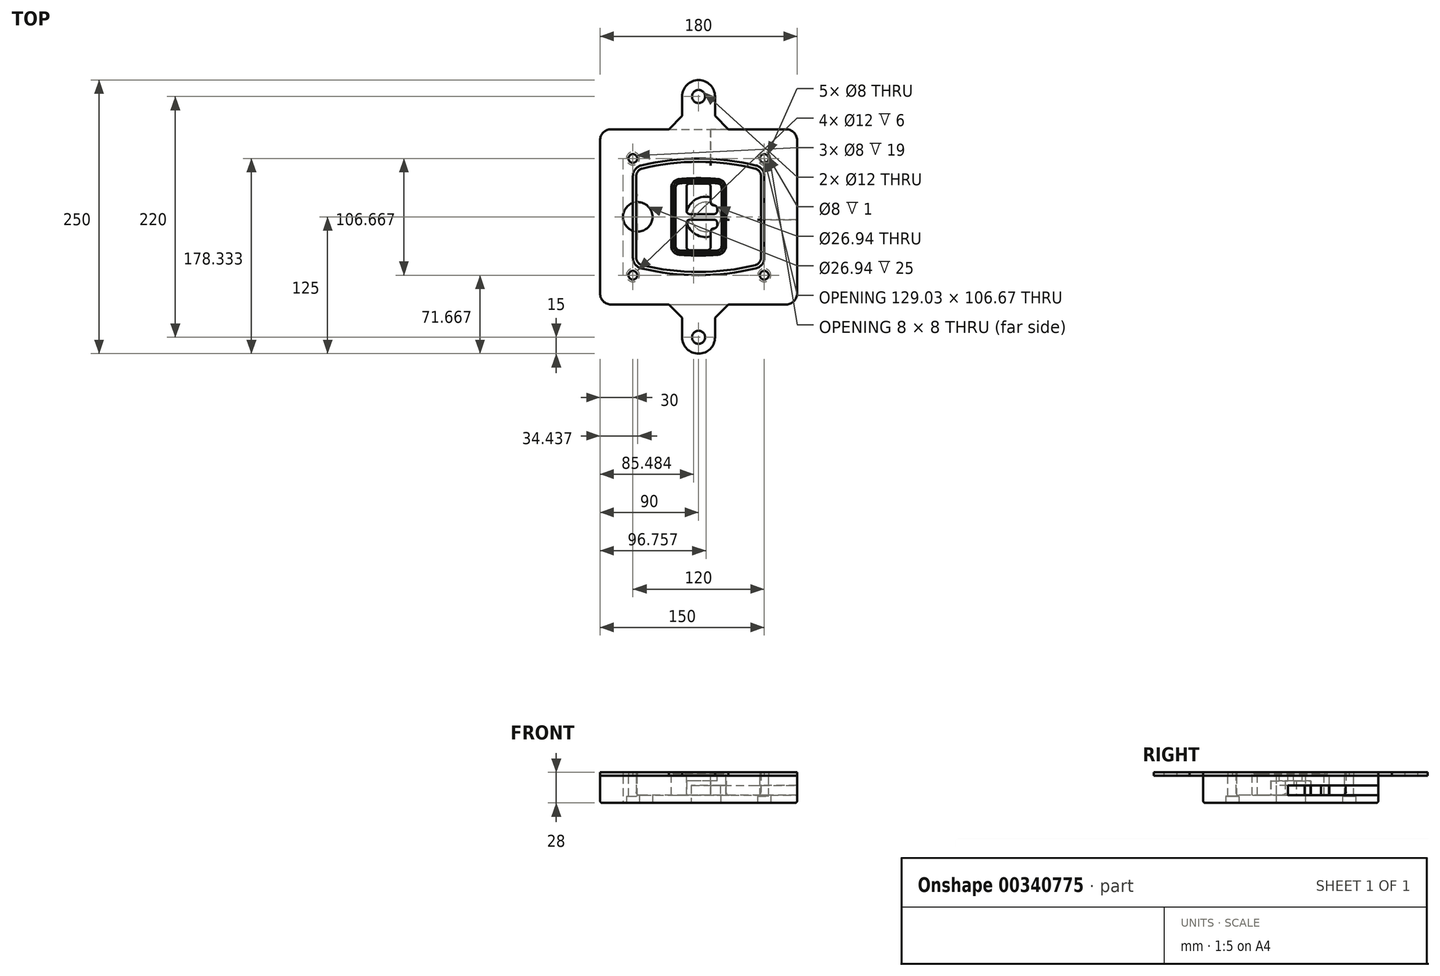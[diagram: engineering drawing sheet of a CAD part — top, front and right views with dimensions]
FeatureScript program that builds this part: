
annotation { "Feature Type Name" : "Feature", "Feature Type Description" : "" }
export const myFeature = defineFeature(function(context is Context, id is Id, definition is map)
    precondition{}
    {
        {
            var Q0;
            Q0=qCreatedBy(makeId("Top.planeOp"),FACE);
            var sketch = newSketch(context, id + "F0", { "sketchPlane" : qUnion([Q0])});
            skPoint(sketch, "E0.rect.middle", {"position": v(0, 0) * mm});
            skLineSegment(sketch, "E1.bottom", {"start": v(-80, -80) * mm, "end": v(80, -80) * mm});
            skLineSegment(sketch, "E1.top", {"start": v(-80, 80) * mm, "end": v(80, 80) * mm});
            skLineSegment(sketch, "E1.left", {"start": v(-90, -70) * mm, "end": v(-90, 70) * mm});
            skLineSegment(sketch, "E1.right", {"start": v(90, -70) * mm, "end": v(90, 70) * mm});
            skLineSegment(sketch, "E2", {"start": v(-90, 80) * mm, "end": v(90, -80) * mm, "construction": true});
            skLineSegment(sketch, "E3", {"start": v(90, 80) * mm, "end": v(-90, -80) * mm, "construction": true});
            skCircle(sketch, "E4", {"center": v(-60, 53.33) * mm, "radius": 4 * mm});
            skCircle(sketch, "E5", {"center": v(60, 53.33) * mm, "radius": 4 * mm});
            skCircle(sketch, "E6", {"center": v(60, -53.33) * mm, "radius": 4 * mm});
            skCircle(sketch, "E7", {"center": v(-60, -53.33) * mm, "radius": 4 * mm});
            skLineSegment(sketch, "E8", {"start": v(-60, 53.33) * mm, "end": v(60, 53.33) * mm, "construction": true});
            skLineSegment(sketch, "E9", {"start": v(60, 53.33) * mm, "end": v(60, -53.33) * mm, "construction": true});
            skLineSegment(sketch, "E10", {"start": v(60, -53.33) * mm, "end": v(-60, -53.33) * mm, "construction": true});
            skLineSegment(sketch, "E11", {"start": v(-60, -53.33) * mm, "end": v(-60, 53.33) * mm, "construction": true});
            skLineSegment(sketch, "E12", {"start": v(-60, 37.3) * mm, "end": v(-60, -37.3) * mm});
            skLineSegment(sketch, "E13", {"start": v(60, 37.3) * mm, "end": v(60, -37.3) * mm});
            skArc(sketch, "E14", {"start": v(52.38, 47.01) * mm, "mid": v(0, 53.33) * mm, "end": v(-52.38, 47.01) * mm});
            skArc(sketch, "E15", {"start": v(-52.38, -47.01) * mm, "mid": v(0, -53.33) * mm, "end": v(52.38, -47.01) * mm});
            skLineSegment(sketch, "E16", {"start": v(-60, 0) * mm, "end": v(60, 0) * mm, "construction": true});
            skPoint(sketch, "E17.visualSharp", {"position": v(-60, -45) * mm});
            skArc(sketch, "E17.filletArc", {"start": v(-60, -37.3) * mm, "mid": v(-57.87, -43.47) * mm, "end": v(-52.38, -47.01) * mm});
            skPoint(sketch, "E18.visualSharp", {"position": v(-60, 45) * mm});
            skArc(sketch, "E18.filletArc", {"start": v(-52.38, 47.01) * mm, "mid": v(-57.87, 43.47) * mm, "end": v(-60, 37.3) * mm});
            skPoint(sketch, "E19.visualSharp", {"position": v(60, 45) * mm});
            skArc(sketch, "E19.filletArc", {"start": v(60, 37.3) * mm, "mid": v(57.87, 43.47) * mm, "end": v(52.38, 47.01) * mm});
            skPoint(sketch, "E20.visualSharp", {"position": v(60, -45) * mm});
            skArc(sketch, "E20.filletArc", {"start": v(52.38, -47.01) * mm, "mid": v(57.87, -43.47) * mm, "end": v(60, -37.3) * mm});
            skPoint(sketch, "E21.visualSharp", {"position": v(-90, 80) * mm});
            skArc(sketch, "E21.filletArc", {"start": v(-80, 80) * mm, "mid": v(-87.07, 77.07) * mm, "end": v(-90, 70) * mm});
            skPoint(sketch, "E22.visualSharp", {"position": v(90, 80) * mm});
            skArc(sketch, "E22.filletArc", {"start": v(90, 70) * mm, "mid": v(87.07, 77.07) * mm, "end": v(80, 80) * mm});
            skPoint(sketch, "E23.visualSharp", {"position": v(90, -80) * mm});
            skArc(sketch, "E23.filletArc", {"start": v(80, -80) * mm, "mid": v(87.07, -77.07) * mm, "end": v(90, -70) * mm});
            skPoint(sketch, "E24.visualSharp", {"position": v(-90, -80) * mm});
            skArc(sketch, "E24.filletArc", {"start": v(-90, -70) * mm, "mid": v(-87.07, -77.07) * mm, "end": v(-80, -80) * mm});
            skArc(sketch, "E25.0", {"start": v(57, 37.3) * mm, "mid": v(55.5, 41.62) * mm, "end": v(51.67, 44.1) * mm});
            skLineSegment(sketch, "E25.1", {"start": v(57, 37.3) * mm, "end": v(57, -37.3) * mm});
            skArc(sketch, "E25.2", {"start": v(51.67, -44.1) * mm, "mid": v(55.5, -41.62) * mm, "end": v(57, -37.3) * mm});
            skArc(sketch, "E25.3", {"start": v(-51.67, -44.1) * mm, "mid": v(0, -50.33) * mm, "end": v(51.67, -44.1) * mm});
            skArc(sketch, "E25.4", {"start": v(-57, -37.3) * mm, "mid": v(-55.5, -41.62) * mm, "end": v(-51.67, -44.1) * mm});
            skArc(sketch, "E25.5", {"start": v(51.67, 44.1) * mm, "mid": v(0, 50.33) * mm, "end": v(-51.67, 44.1) * mm});
            skLineSegment(sketch, "E25.6", {"start": v(-57, 37.3) * mm, "end": v(-57, -37.3) * mm});
            skArc(sketch, "E25.7", {"start": v(-51.67, 44.1) * mm, "mid": v(-55.5, 41.62) * mm, "end": v(-57, 37.3) * mm});
            skArc(sketch, "E26.0", {"start": v(-53.33, 50.9) * mm, "mid": v(-61.01, 45.94) * mm, "end": v(-64, 37.3) * mm});
            skArc(sketch, "E26.1", {"start": v(53.33, 50.9) * mm, "mid": v(0, 57.33) * mm, "end": v(-53.33, 50.9) * mm});
            skArc(sketch, "E26.2", {"start": v(64, 37.3) * mm, "mid": v(61.01, 45.94) * mm, "end": v(53.33, 50.9) * mm});
            skLineSegment(sketch, "E26.3", {"start": v(64, 37.3) * mm, "end": v(64, -37.3) * mm});
            skArc(sketch, "E26.4", {"start": v(53.33, -50.9) * mm, "mid": v(61.01, -45.94) * mm, "end": v(64, -37.3) * mm});
            skLineSegment(sketch, "E26.5", {"start": v(-64, 37.3) * mm, "end": v(-64, -37.3) * mm});
            skArc(sketch, "E26.6", {"start": v(-53.33, -50.9) * mm, "mid": v(0, -57.33) * mm, "end": v(53.33, -50.9) * mm});
            skArc(sketch, "E26.7", {"start": v(-64, -37.3) * mm, "mid": v(-61.01, -45.94) * mm, "end": v(-53.33, -50.9) * mm});
            skSolve(sketch);
        }
        {
            var Q0;
            Q0=makeQuery(id+"F0.imprint","IMPRINT",FACE,{"disambiguationData":[TD([[makeQuery(id+"F0.imprint","IMPRINT",EDGE,{"derivedFrom":sQuery(id+"F0.wireOp",EDGE,"E1.bottom")}),1.0]])]});
            var Q1;
            Q1=makeQuery(id+"F0.imprint","IMPRINT",FACE,{"disambiguationData":[TD([[makeQuery(id+"F0.imprint","IMPRINT",EDGE,{"derivedFrom":sQuery(id+"F0.wireOp",EDGE,"E12")}),1.0]])]});
            var Q2;
            Q2=makeQuery(id+"F0.imprint","IMPRINT",FACE,{"disambiguationData":[TD([[makeQuery(id+"F0.imprint","IMPRINT",EDGE,{"derivedFrom":sQuery(id+"F0.wireOp",EDGE,"E25.0")}),1.0]])]});
            var Q3;
            Q3=makeQuery(id+"F0.imprint","IMPRINT",FACE,{"disambiguationData":[TD([[makeQuery(id+"F0.imprint","IMPRINT",EDGE,{"derivedFrom":sQuery(id+"F0.wireOp",EDGE,"E12")}),-1.0]])]});
            extrude(context, id + "F1", {"entities" : qUnion([Q0, Q1, Q2, Q3]), "oppositeDirection" : true, "depth" : 25 * mm});
        }
        {
            var Q0;
            Q0=makeQuery(id+"F0.imprint","IMPRINT",FACE,{"disambiguationData":[TD([[makeQuery(id+"F0.imprint","IMPRINT",EDGE,{"derivedFrom":sQuery(id+"F0.wireOp",EDGE,"E12")}),1.0]])]});
            extrude(context, id + "F2", {"entities" : qUnion([Q0]), "operationType" : NewBodyOperationType.ADD, "depth" : 3 * mm});
        }
        {
            var Q0;
            Q0=makeQuery(id+"F0.imprint","IMPRINT",FACE,{"disambiguationData":[TD([[makeQuery(id+"F0.imprint","IMPRINT",EDGE,{"derivedFrom":sQuery(id+"F0.wireOp",EDGE,"E25.0")}),1.0]])]});
            extrude(context, id + "F3", {"entities" : qUnion([Q0]), "operationType" : NewBodyOperationType.REMOVE, "oppositeDirection" : true, "depth" : 18 * mm});
        }
        {
            var Q0;
            Q0=makeQuery(id+"F2.opExtrude","CAP_FACE",FACE,{"disambiguationData":[OSD([sQuery(id+"F0.wireOp",EDGE,"E12"),sQuery(id+"F0.wireOp",EDGE,"E13"),sQuery(id+"F0.wireOp",EDGE,"E14"),sQuery(id+"F0.wireOp",EDGE,"E15"),sQuery(id+"F0.wireOp",EDGE,"E17.filletArc"),sQuery(id+"F0.wireOp",EDGE,"E18.filletArc"),sQuery(id+"F0.wireOp",EDGE,"E19.filletArc"),sQuery(id+"F0.wireOp",EDGE,"E20.filletArc"),sQuery(id+"F0.wireOp",EDGE,"E25.0"),sQuery(id+"F0.wireOp",EDGE,"E25.1"),sQuery(id+"F0.wireOp",EDGE,"E25.2"),sQuery(id+"F0.wireOp",EDGE,"E25.3"),sQuery(id+"F0.wireOp",EDGE,"E25.4"),sQuery(id+"F0.wireOp",EDGE,"E25.5"),sQuery(id+"F0.wireOp",EDGE,"E25.6"),sQuery(id+"F0.wireOp",EDGE,"E25.7")])],"isStart":false});
            var sketch = newSketch(context, id + "F4", { "sketchPlane" : qUnion([Q0])});
            skArc(sketch, "E27.0", {"start": v(-17.7, -34.56) * mm, "mid": v(0, -35.33) * mm, "end": v(17.7, -34.56) * mm});
            skArc(sketch, "E28.0", {"start": v(17.7, 34.56) * mm, "mid": v(0, 35.33) * mm, "end": v(-17.7, 34.56) * mm});
            skLineSegment(sketch, "E29", {"start": v(-25, 26.59) * mm, "end": v(-25, -26.59) * mm});
            skLineSegment(sketch, "E30", {"start": v(25, 26.59) * mm, "end": v(25, -26.59) * mm});
            skLineSegment(sketch, "E31", {"start": v(-25, 33.78) * mm, "end": v(25, 33.78) * mm, "construction": true});
            skLineSegment(sketch, "E32", {"start": v(-25, -33.78) * mm, "end": v(25, -33.78) * mm, "construction": true});
            skPoint(sketch, "E33.visualSharp", {"position": v(-25, 33.78) * mm});
            skArc(sketch, "E33.filletArc", {"start": v(-17.7, 34.56) * mm, "mid": v(-22.9, 32) * mm, "end": v(-25, 26.59) * mm});
            skPoint(sketch, "E34.visualSharp", {"position": v(25, 33.78) * mm});
            skArc(sketch, "E34.filletArc", {"start": v(25, 26.59) * mm, "mid": v(22.9, 32) * mm, "end": v(17.7, 34.56) * mm});
            skPoint(sketch, "E35.visualSharp", {"position": v(25, -33.78) * mm});
            skArc(sketch, "E35.filletArc", {"start": v(17.7, -34.56) * mm, "mid": v(22.9, -32) * mm, "end": v(25, -26.59) * mm});
            skPoint(sketch, "E36.visualSharp", {"position": v(-25, -33.78) * mm});
            skArc(sketch, "E36.filletArc", {"start": v(-25, -26.59) * mm, "mid": v(-22.9, -32) * mm, "end": v(-17.7, -34.56) * mm});
            skArc(sketch, "E37.0", {"start": v(51.67, 44.1) * mm, "mid": v(0, 50.33) * mm, "end": v(-51.67, 44.1) * mm});
            skArc(sketch, "E37.1", {"start": v(-51.67, 44.1) * mm, "mid": v(-55.5, 41.62) * mm, "end": v(-57, 37.3) * mm});
            skLineSegment(sketch, "E37.2", {"start": v(-57, 37.3) * mm, "end": v(-57, -37.3) * mm});
            skArc(sketch, "E37.3", {"start": v(-57, -37.3) * mm, "mid": v(-55.5, -41.62) * mm, "end": v(-51.67, -44.1) * mm});
            skArc(sketch, "E37.4", {"start": v(-51.67, -44.1) * mm, "mid": v(0, -50.33) * mm, "end": v(51.67, -44.1) * mm});
            skArc(sketch, "E37.5", {"start": v(51.67, -44.1) * mm, "mid": v(55.5, -41.62) * mm, "end": v(57, -37.3) * mm});
            skLineSegment(sketch, "E37.6", {"start": v(57, 37.3) * mm, "end": v(57, -37.3) * mm});
            skArc(sketch, "E37.7", {"start": v(57, 37.3) * mm, "mid": v(55.5, 41.62) * mm, "end": v(51.67, 44.1) * mm});
            skLineSegment(sketch, "E38.0", {"start": v(23, 26.59) * mm, "end": v(23, -26.59) * mm});
            skArc(sketch, "E38.1", {"start": v(17.53, -32.56) * mm, "mid": v(21.42, -30.64) * mm, "end": v(23, -26.59) * mm});
            skArc(sketch, "E38.2", {"start": v(-17.53, -32.56) * mm, "mid": v(0, -33.33) * mm, "end": v(17.53, -32.56) * mm});
            skArc(sketch, "E38.3", {"start": v(-23, -26.59) * mm, "mid": v(-21.42, -30.64) * mm, "end": v(-17.53, -32.56) * mm});
            skLineSegment(sketch, "E38.4", {"start": v(-23, 26.59) * mm, "end": v(-23, -26.59) * mm});
            skArc(sketch, "E38.5", {"start": v(23, 26.59) * mm, "mid": v(21.42, 30.64) * mm, "end": v(17.53, 32.56) * mm});
            skArc(sketch, "E38.6", {"start": v(-17.53, 32.56) * mm, "mid": v(-21.42, 30.64) * mm, "end": v(-23, 26.59) * mm});
            skArc(sketch, "E38.7", {"start": v(17.53, 32.56) * mm, "mid": v(0, 33.33) * mm, "end": v(-17.53, 32.56) * mm});
            skArc(sketch, "E39.0", {"start": v(21, 26.59) * mm, "mid": v(19.95, 29.29) * mm, "end": v(17.35, 30.57) * mm});
            skLineSegment(sketch, "E39.1", {"start": v(21, 26.59) * mm, "end": v(21, -26.59) * mm});
            skArc(sketch, "E39.2", {"start": v(17.35, -30.57) * mm, "mid": v(19.95, -29.29) * mm, "end": v(21, -26.59) * mm});
            skArc(sketch, "E39.3", {"start": v(-17.35, -30.57) * mm, "mid": v(0, -31.33) * mm, "end": v(17.35, -30.57) * mm});
            skArc(sketch, "E39.4", {"start": v(-21, -26.59) * mm, "mid": v(-19.95, -29.29) * mm, "end": v(-17.35, -30.57) * mm});
            skArc(sketch, "E39.5", {"start": v(17.35, 30.57) * mm, "mid": v(0, 31.33) * mm, "end": v(-17.35, 30.57) * mm});
            skLineSegment(sketch, "E39.6", {"start": v(-21, 26.59) * mm, "end": v(-21, -26.59) * mm});
            skArc(sketch, "E39.7", {"start": v(-17.35, 30.57) * mm, "mid": v(-19.95, 29.29) * mm, "end": v(-21, 26.59) * mm});
            skLineSegment(sketch, "E40", {"start": v(-25, 0) * mm, "end": v(25, 0) * mm, "construction": true});
            skLineSegment(sketch, "E41", {"start": v(-11, 5.5) * mm, "end": v(-11, 27.5) * mm});
            skLineSegment(sketch, "E42", {"start": v(-8, 30.5) * mm, "end": v(8, 30.5) * mm});
            skLineSegment(sketch, "E43", {"start": v(11, 27.5) * mm, "end": v(11, 13.5) * mm});
            skLineSegment(sketch, "E44", {"start": v(14, 10.5) * mm, "end": v(14, 10.5) * mm});
            skLineSegment(sketch, "E45", {"start": v(17, 7.5) * mm, "end": v(17, 5.5) * mm});
            skLineSegment(sketch, "E46", {"start": v(14, 2.5) * mm, "end": v(-8, 2.5) * mm});
            skPoint(sketch, "E47.visualSharp", {"position": v(-11, 30.5) * mm});
            skArc(sketch, "E47.filletArc", {"start": v(-8, 30.5) * mm, "mid": v(-10.12, 29.62) * mm, "end": v(-11, 27.5) * mm});
            skPoint(sketch, "E48.visualSharp", {"position": v(11, 30.5) * mm});
            skArc(sketch, "E48.filletArc", {"start": v(11, 27.5) * mm, "mid": v(10.12, 29.62) * mm, "end": v(8, 30.5) * mm});
            skPoint(sketch, "E49.visualSharp", {"position": v(11, 10.5) * mm});
            skArc(sketch, "E49.filletArc", {"start": v(11, 13.5) * mm, "mid": v(11.88, 11.38) * mm, "end": v(14, 10.5) * mm});
            skPoint(sketch, "E50.visualSharp", {"position": v(17, 10.5) * mm});
            skArc(sketch, "E50.filletArc", {"start": v(17, 7.5) * mm, "mid": v(16.12, 9.62) * mm, "end": v(14, 10.5) * mm});
            skPoint(sketch, "E51.visualSharp", {"position": v(17, 2.5) * mm});
            skArc(sketch, "E51.filletArc", {"start": v(14, 2.5) * mm, "mid": v(16.12, 3.38) * mm, "end": v(17, 5.5) * mm});
            skPoint(sketch, "E52.visualSharp", {"position": v(-11, 2.5) * mm});
            skArc(sketch, "E52.filletArc", {"start": v(-11, 5.5) * mm, "mid": v(-10.12, 3.38) * mm, "end": v(-8, 2.5) * mm});
            skLineSegment(sketch, "E53.0.MirrorCS", {"start": v(14, -2.5) * mm, "end": v(-8, -2.5) * mm});
            skArc(sketch, "E54.0.MirrorCS", {"start": v(-11, -5.5) * mm, "mid": v(-10.12, -3.38) * mm, "end": v(-8, -2.5) * mm});
            skLineSegment(sketch, "E55.0.MirrorCS", {"start": v(-11, -5.5) * mm, "end": v(-11, -27.5) * mm});
            skArc(sketch, "E56.0.MirrorCS", {"start": v(-8, -30.5) * mm, "mid": v(-10.12, -29.62) * mm, "end": v(-11, -27.5) * mm});
            skLineSegment(sketch, "E57.0.MirrorCS", {"start": v(-8, -30.5) * mm, "end": v(8, -30.5) * mm});
            skArc(sketch, "E58.0.MirrorCS", {"start": v(11, -27.5) * mm, "mid": v(10.12, -29.62) * mm, "end": v(8, -30.5) * mm});
            skLineSegment(sketch, "E59.0.MirrorCS", {"start": v(11, -27.5) * mm, "end": v(11, -13.5) * mm});
            skArc(sketch, "E60.0.MirrorCS", {"start": v(11, -13.5) * mm, "mid": v(11.88, -11.38) * mm, "end": v(14, -10.5) * mm});
            skArc(sketch, "E61.0.MirrorCS", {"start": v(17, -7.5) * mm, "mid": v(16.12, -9.62) * mm, "end": v(14, -10.5) * mm});
            skLineSegment(sketch, "E62.0.MirrorCS", {"start": v(17, -7.5) * mm, "end": v(17, -5.5) * mm});
            skArc(sketch, "E63.0.MirrorCS", {"start": v(14, -2.5) * mm, "mid": v(16.12, -3.38) * mm, "end": v(17, -5.5) * mm});
            skSolve(sketch);
        }
        {
            var Q0;
            Q0=makeQuery(id+"F4.imprint","IMPRINT",FACE,{"disambiguationData":[TD([[makeQuery(id+"F4.imprint","IMPRINT",EDGE,{"derivedFrom":sQuery(id+"F4.wireOp",EDGE,"E27.0")}),1.0]])]});
            var Q1;
            Q1=makeQuery(id+"F4.imprint","IMPRINT",FACE,{"disambiguationData":[TD([[makeQuery(id+"F4.imprint","IMPRINT",EDGE,{"derivedFrom":sQuery(id+"F4.wireOp",EDGE,"E38.0")}),-1.0]])]});
            var Q2;
            Q2=makeQuery(id+"F4.imprint","IMPRINT",FACE,{"disambiguationData":[TD([[makeQuery(id+"F4.imprint","IMPRINT",EDGE,{"derivedFrom":sQuery(id+"F4.wireOp",EDGE,"E39.0")}),1.0]])]});
            extrude(context, id + "F5", {"entities" : qUnion([Q0, Q1, Q2]), "operationType" : NewBodyOperationType.ADD, "endBound" : BoundingType.UP_TO_NEXT, "oppositeDirection" : true, "depth" : 25 * mm});
        }
        {
            var Q0;
            Q0=makeQuery(id+"F4.imprint","IMPRINT",FACE,{"disambiguationData":[TD([[makeQuery(id+"F4.imprint","IMPRINT",EDGE,{"derivedFrom":sQuery(id+"F4.wireOp",EDGE,"E38.0")}),-1.0]])]});
            extrude(context, id + "F6", {"entities" : qUnion([Q0]), "operationType" : NewBodyOperationType.REMOVE, "oppositeDirection" : true, "depth" : 2 * mm});
        }
        {
            var Q0;
            Q0=makeQuery(id+"F1.opExtrude","CAP_FACE",FACE,{"disambiguationData":[OSD([sQuery(id+"F0.wireOp",EDGE,"E1.bottom"),sQuery(id+"F0.wireOp",EDGE,"E1.top"),sQuery(id+"F0.wireOp",EDGE,"E1.left"),sQuery(id+"F0.wireOp",EDGE,"E1.right"),sQuery(id+"F0.wireOp",EDGE,"E4"),sQuery(id+"F0.wireOp",EDGE,"E5"),sQuery(id+"F0.wireOp",EDGE,"E6"),sQuery(id+"F0.wireOp",EDGE,"E7"),sQuery(id+"F0.wireOp",EDGE,"E21.filletArc"),sQuery(id+"F0.wireOp",EDGE,"E22.filletArc"),sQuery(id+"F0.wireOp",EDGE,"E23.filletArc"),sQuery(id+"F0.wireOp",EDGE,"E24.filletArc")])],"isStart":false});
            var sketch = newSketch(context, id + "F7", { "sketchPlane" : qUnion([Q0])});
            skCircle(sketch, "E64", {"center": v(6.76, 0) * mm, "radius": 13.47 * mm});
            skCircle(sketch, "E65", {"center": v(-55.56, 0) * mm, "radius": 13.47 * mm});
            skLineSegment(sketch, "E66", {"start": v(90, 0) * mm, "end": v(-90, 0) * mm});
            skCircle(sketch, "E67", {"center": v(6.76, 0) * mm, "radius": 18.47 * mm});
            skCircle(sketch, "E68", {"center": v(60, -53.33) * mm, "radius": 6 * mm});
            skCircle(sketch, "E69", {"center": v(-60, -53.33) * mm, "radius": 6 * mm});
            skCircle(sketch, "E70", {"center": v(-60, 53.33) * mm, "radius": 6 * mm});
            skCircle(sketch, "E71", {"center": v(60, 53.33) * mm, "radius": 6 * mm});
            skSolve(sketch);
        }
        {
            var Q0;
            {var subQ1=sQuery(id+"F7.wireOp",EDGE,"E66");var subQ4=sQuery(id+"F7.wireOp",EDGE,"E64");var subQ6=makeQuery(id+"F7.imprint","INTERSECT",VERTEX,{"disambiguationData":[OD(0.0)],"derivedFrom":[subQ4,subQ1]});Q0=makeQuery(id+"F7.imprint","IMPRINT",FACE,{"disambiguationData":[TD([[makeQuery(id+"F7.imprint","IMPRINT",EDGE,{"disambiguationData":[TD([[subQ6,-1.0]])],"derivedFrom":subQ4}),-1.0]])]});}
            var Q1;
            {var subQ0=sQuery(id+"F7.wireOp",EDGE,"E66");var subQ1=sQuery(id+"F7.wireOp",EDGE,"E64");var subQ3=makeQuery(id+"F7.imprint","INTERSECT",VERTEX,{"disambiguationData":[OD(0.0)],"derivedFrom":[subQ1,subQ0]});Q1=makeQuery(id+"F7.imprint","IMPRINT",FACE,{"disambiguationData":[TD([[makeQuery(id+"F7.imprint","IMPRINT",EDGE,{"disambiguationData":[TD([[subQ3,-1.0]])],"derivedFrom":subQ1}),1.0]])]});}
            var Q2;
            {var subQ0=sQuery(id+"F7.wireOp",EDGE,"E66");var subQ1=sQuery(id+"F7.wireOp",EDGE,"E64");var subQ3=makeQuery(id+"F7.imprint","INTERSECT",VERTEX,{"disambiguationData":[OD(0.0)],"derivedFrom":[subQ1,subQ0]});Q2=makeQuery(id+"F7.imprint","IMPRINT",FACE,{"disambiguationData":[TD([[makeQuery(id+"F7.imprint","IMPRINT",EDGE,{"disambiguationData":[TD([[subQ3,1.0]])],"derivedFrom":subQ1}),1.0]])]});}
            var Q3;
            {var subQ1=sQuery(id+"F7.wireOp",EDGE,"E66");var subQ4=sQuery(id+"F7.wireOp",EDGE,"E64");var subQ6=makeQuery(id+"F7.imprint","INTERSECT",VERTEX,{"disambiguationData":[OD(0.0)],"derivedFrom":[subQ4,subQ1]});Q3=makeQuery(id+"F7.imprint","IMPRINT",FACE,{"disambiguationData":[TD([[makeQuery(id+"F7.imprint","IMPRINT",EDGE,{"disambiguationData":[TD([[subQ6,1.0]])],"derivedFrom":subQ4}),-1.0]])]});}
            extrude(context, id + "F8", {"entities" : qUnion([Q0, Q1, Q2, Q3]), "operationType" : NewBodyOperationType.ADD, "oppositeDirection" : true, "depth" : 20 * mm});
        }
        {
            var Q0;
            {var subQ0=sQuery(id+"F7.wireOp",EDGE,"E66");var subQ1=sQuery(id+"F7.wireOp",EDGE,"E64");var subQ3=makeQuery(id+"F7.imprint","INTERSECT",VERTEX,{"disambiguationData":[OD(0.0)],"derivedFrom":[subQ1,subQ0]});Q0=makeQuery(id+"F7.imprint","IMPRINT",FACE,{"disambiguationData":[TD([[makeQuery(id+"F7.imprint","IMPRINT",EDGE,{"disambiguationData":[TD([[subQ3,-1.0]])],"derivedFrom":subQ1}),1.0]])]});}
            var Q1;
            {var subQ0=sQuery(id+"F7.wireOp",EDGE,"E66");var subQ1=sQuery(id+"F7.wireOp",EDGE,"E64");var subQ3=makeQuery(id+"F7.imprint","INTERSECT",VERTEX,{"disambiguationData":[OD(0.0)],"derivedFrom":[subQ1,subQ0]});Q1=makeQuery(id+"F7.imprint","IMPRINT",FACE,{"disambiguationData":[TD([[makeQuery(id+"F7.imprint","IMPRINT",EDGE,{"disambiguationData":[TD([[subQ3,1.0]])],"derivedFrom":subQ1}),1.0]])]});}
            extrude(context, id + "F9", {"entities" : qUnion([Q0, Q1]), "operationType" : NewBodyOperationType.REMOVE, "oppositeDirection" : true, "depth" : 16 * mm});
        }
        {
            var Q0;
            {var subQ0=sQuery(id+"F7.wireOp",EDGE,"E66");var subQ1=sQuery(id+"F7.wireOp",EDGE,"E65");var subQ3=makeQuery(id+"F7.imprint","INTERSECT",VERTEX,{"disambiguationData":[OD(0.0)],"derivedFrom":[subQ1,subQ0]});Q0=makeQuery(id+"F7.imprint","IMPRINT",FACE,{"disambiguationData":[TD([[makeQuery(id+"F7.imprint","IMPRINT",EDGE,{"disambiguationData":[TD([[subQ3,-1.0]])],"derivedFrom":subQ1}),1.0]])]});}
            var Q1;
            {var subQ0=sQuery(id+"F7.wireOp",EDGE,"E66");var subQ1=sQuery(id+"F7.wireOp",EDGE,"E65");var subQ3=makeQuery(id+"F7.imprint","INTERSECT",VERTEX,{"disambiguationData":[OD(0.0)],"derivedFrom":[subQ1,subQ0]});Q1=makeQuery(id+"F7.imprint","IMPRINT",FACE,{"disambiguationData":[TD([[makeQuery(id+"F7.imprint","IMPRINT",EDGE,{"disambiguationData":[TD([[subQ3,1.0]])],"derivedFrom":subQ1}),1.0]])]});}
            extrude(context, id + "F10", {"entities" : qUnion([Q0, Q1]), "operationType" : NewBodyOperationType.REMOVE, "oppositeDirection" : true, "depth" : 25 * mm});
        }
        {
            var Q0;
            Q0=makeQuery(id+"F7.imprint","IMPRINT",FACE,{"disambiguationData":[TD([[makeQuery(id+"F7.imprint","IMPRINT",EDGE,{"derivedFrom":sQuery(id+"F7.wireOp",EDGE,"E68")}),1.0]])]});
            var Q1;
            Q1=makeQuery(id+"F7.imprint","IMPRINT",FACE,{"disambiguationData":[TD([[makeQuery(id+"F7.imprint","IMPRINT",EDGE,{"derivedFrom":makeQuery(id+"F1.opExtrude","CAP_EDGE",EDGE,{"disambiguationData":[OSD([sQuery(id+"F0.wireOp",EDGE,"E5")])],"isStart":false})}),-1.0]])]});
            var Q2;
            Q2=makeQuery(id+"F7.imprint","IMPRINT",FACE,{"disambiguationData":[TD([[makeQuery(id+"F7.imprint","IMPRINT",EDGE,{"derivedFrom":sQuery(id+"F7.wireOp",EDGE,"E69")}),1.0]])]});
            var Q3;
            Q3=makeQuery(id+"F7.imprint","IMPRINT",FACE,{"disambiguationData":[TD([[makeQuery(id+"F7.imprint","IMPRINT",EDGE,{"derivedFrom":makeQuery(id+"F1.opExtrude","CAP_EDGE",EDGE,{"disambiguationData":[OSD([sQuery(id+"F0.wireOp",EDGE,"E4")])],"isStart":false})}),-1.0]])]});
            var Q4;
            Q4=makeQuery(id+"F7.imprint","IMPRINT",FACE,{"disambiguationData":[TD([[makeQuery(id+"F7.imprint","IMPRINT",EDGE,{"derivedFrom":sQuery(id+"F7.wireOp",EDGE,"E70")}),1.0]])]});
            var Q5;
            Q5=makeQuery(id+"F7.imprint","IMPRINT",FACE,{"disambiguationData":[TD([[makeQuery(id+"F7.imprint","IMPRINT",EDGE,{"derivedFrom":makeQuery(id+"F1.opExtrude","CAP_EDGE",EDGE,{"disambiguationData":[OSD([sQuery(id+"F0.wireOp",EDGE,"E7")])],"isStart":false})}),-1.0]])]});
            var Q6;
            Q6=makeQuery(id+"F7.imprint","IMPRINT",FACE,{"disambiguationData":[TD([[makeQuery(id+"F7.imprint","IMPRINT",EDGE,{"derivedFrom":sQuery(id+"F7.wireOp",EDGE,"E71")}),1.0]])]});
            var Q7;
            Q7=makeQuery(id+"F7.imprint","IMPRINT",FACE,{"disambiguationData":[TD([[makeQuery(id+"F7.imprint","IMPRINT",EDGE,{"derivedFrom":makeQuery(id+"F1.opExtrude","CAP_EDGE",EDGE,{"disambiguationData":[OSD([sQuery(id+"F0.wireOp",EDGE,"E6")])],"isStart":false})}),-1.0]])]});
            extrude(context, id + "F11", {"entities" : qUnion([Q0, Q1, Q2, Q3, Q4, Q5, Q6, Q7]), "operationType" : NewBodyOperationType.REMOVE, "oppositeDirection" : true, "depth" : 6 * mm});
        }
        {
            var Q0;
            Q0=makeQuery(id+"F9.boolean.opBoolean","COPY",FACE,{"derivedFrom":makeQuery(id+"F9.opExtrude","CAP_FACE",FACE,{"disambiguationData":[OSD([sQuery(id+"F7.wireOp",EDGE,"E64")])],"isStart":false})});
            var sketch = newSketch(context, id + "F12", { "sketchPlane" : qUnion([Q0])});
            skArc(sketch, "E72.0", {"start": v(11, -88.19) * mm, "mid": v(97.1, -83.6) * mm, "end": v(92.5, 2.5) * mm});
            skLineSegment(sketch, "E72.1", {"start": v(11, -17.97) * mm, "end": v(11, -17.97) * mm});
            skLineSegment(sketch, "E73", {"start": v(92.5, -105.13) * mm, "end": v(102.3, -105.13) * mm});
            skLineSegment(sketch, "E74.0", {"start": v(92.5, 2.5) * mm, "end": v(14, 2.5) * mm});
            skArc(sketch, "E74.1", {"start": v(14, 2.5) * mm, "mid": v(16.12, 3.38) * mm, "end": v(17, 5.5) * mm});
            skLineSegment(sketch, "E74.2", {"start": v(17, 7.5) * mm, "end": v(17, 5.5) * mm});
            skArc(sketch, "E74.3", {"start": v(17, 7.5) * mm, "mid": v(16.12, 9.62) * mm, "end": v(14, 10.5) * mm});
            skArc(sketch, "E74.4", {"start": v(11, 13.5) * mm, "mid": v(11.88, 11.38) * mm, "end": v(14, 10.5) * mm});
            skLineSegment(sketch, "E74.5", {"start": v(11, 13.5) * mm, "end": v(11, -88.19) * mm});
            skLineSegment(sketch, "E74.7", {"start": v(92.5, -2.5) * mm, "end": v(14, -2.5) * mm});
            skArc(sketch, "E74.8", {"start": v(14, -2.5) * mm, "mid": v(16.12, -3.38) * mm, "end": v(17, -5.5) * mm});
            skLineSegment(sketch, "E74.9", {"start": v(17, -7.5) * mm, "end": v(17, -5.5) * mm});
            skArc(sketch, "E74.10", {"start": v(17, -7.5) * mm, "mid": v(16.12, -9.62) * mm, "end": v(14, -10.5) * mm});
            skArc(sketch, "E74.11", {"start": v(11, -13.5) * mm, "mid": v(11.88, -11.38) * mm, "end": v(14, -10.5) * mm});
            skLineSegment(sketch, "E74.12", {"start": v(11, -17.97) * mm, "end": v(11, -13.5) * mm});
            skPoint(sketch, "E75.orphan", {"position": v(11, -27.5) * mm});
            skPoint(sketch, "E76.orphan", {"position": v(-8, -2.5) * mm});
            skPoint(sketch, "E77.orphan", {"position": v(-8, 2.5) * mm});
            skPoint(sketch, "E78.orphan", {"position": v(11, 27.5) * mm});
            skSolve(sketch);
        }
        {
            var Q0;
            {var subQ7=sQuery(id+"F12.wireOp",EDGE,"E72.0");var subQ14=sQuery(id+"F12.wireOp",EDGE,"E72.1");var subQ16=sQuery(id+"F12.wireOp",EDGE,"E74.1");var subQ18=sQuery(id+"F12.wireOp",EDGE,"E74.8");Q0=qUnion([makeQuery(id+"F12.imprint","IMPRINT",FACE,{"disambiguationData":[TD([[makeQuery(id+"F12.imprint","IMPRINT",EDGE,{"derivedFrom":subQ7}),1.0]])]}),makeQuery(id+"F12.imprint","IMPRINT",FACE,{"disambiguationData":[TD([[makeQuery(id+"F12.imprint","IMPRINT",EDGE,{"derivedFrom":subQ14}),1.0]])]}),makeQuery(id+"F12.imprint","IMPRINT",FACE,{"disambiguationData":[TD([[makeQuery(id+"F12.imprint","IMPRINT",EDGE,{"derivedFrom":subQ16}),1.0]])]}),makeQuery(id+"F12.imprint","IMPRINT",FACE,{"disambiguationData":[TD([[makeQuery(id+"F12.imprint","IMPRINT",EDGE,{"derivedFrom":subQ18}),-1.0]])]})]);}
            var Q1;
            Q1=makeQuery(id+"F5.boolean.opBoolean","SPLIT",FACE,{"disambiguationData":[TD([makeQuery(id+"F5.opExtrude","SWEPT_FACE",FACE,{"disambiguationData":[OSD([sQuery(id+"F4.wireOp",EDGE,"E41")])]})])],"derivedFrom":makeQuery(id+"F3.boolean.opBoolean","COPY",FACE,{"derivedFrom":makeQuery(id+"F3.opExtrude","CAP_FACE",FACE,{"disambiguationData":[OSD([sQuery(id+"F0.wireOp",EDGE,"E25.0"),sQuery(id+"F0.wireOp",EDGE,"E25.1"),sQuery(id+"F0.wireOp",EDGE,"E25.2"),sQuery(id+"F0.wireOp",EDGE,"E25.3"),sQuery(id+"F0.wireOp",EDGE,"E25.4"),sQuery(id+"F0.wireOp",EDGE,"E25.5"),sQuery(id+"F0.wireOp",EDGE,"E25.6"),sQuery(id+"F0.wireOp",EDGE,"E25.7")])],"isStart":false})})});
            extrude(context, id + "F13", {"entities" : qUnion([Q0]), "operationType" : NewBodyOperationType.REMOVE, "endBound" : BoundingType.UP_TO_SURFACE, "endBoundEntityFace" : qUnion([Q1]), "depth" : 25 * mm});
        }
        {
            var Q0;
            Q0=makeQuery(id+"F3.boolean.opBoolean","COPY",EDGE,{"derivedFrom":makeQuery(id+"F3.opExtrude","CAP_EDGE",EDGE,{"disambiguationData":[OSD([sQuery(id+"F0.wireOp",EDGE,"E25.6")])],"isStart":false})});
            var Q1;
            Q1=makeQuery(id+"F8.boolean.opBoolean","INTERSECT",EDGE,{"derivedFrom":[makeQuery(id+"F5.opExtrude","SWEPT_FACE",FACE,{"disambiguationData":[OSD([sQuery(id+"F4.wireOp",EDGE,"E30")])]}),makeQuery(id+"F8.opExtrude","CAP_FACE",FACE,{"disambiguationData":[OSD([sQuery(id+"F7.wireOp",EDGE,"E67")])],"isStart":false})]});
            var Q2;
            Q2=makeQuery(id+"F8.boolean.opBoolean","INTERSECT",EDGE,{"disambiguationData":[OD(1.0)],"derivedFrom":[makeQuery(id+"F5.opExtrude","SWEPT_FACE",FACE,{"disambiguationData":[OSD([sQuery(id+"F4.wireOp",EDGE,"E30")])]}),makeQuery(id+"F8.opExtrude","SWEPT_FACE",FACE,{"disambiguationData":[OSD([sQuery(id+"F7.wireOp",EDGE,"E67")])]})]});
            var Q3;
            {var subQ0=makeQuery(id+"F3.boolean.opBoolean","COPY",FACE,{"derivedFrom":makeQuery(id+"F3.opExtrude","CAP_FACE",FACE,{"disambiguationData":[OSD([sQuery(id+"F0.wireOp",EDGE,"E25.0"),sQuery(id+"F0.wireOp",EDGE,"E25.1"),sQuery(id+"F0.wireOp",EDGE,"E25.2"),sQuery(id+"F0.wireOp",EDGE,"E25.3"),sQuery(id+"F0.wireOp",EDGE,"E25.4"),sQuery(id+"F0.wireOp",EDGE,"E25.5"),sQuery(id+"F0.wireOp",EDGE,"E25.6"),sQuery(id+"F0.wireOp",EDGE,"E25.7")])],"isStart":false})});var subQ1=sQuery(id+"F4.wireOp",EDGE,"E30");Q3=makeQuery(id+"F8.boolean.opBoolean","SPLIT",EDGE,{"disambiguationData":[TD([makeQuery(id+"F5.opExtrude","SWEPT_FACE",FACE,{"disambiguationData":[OSD([sQuery(id+"F4.wireOp",EDGE,"E35.filletArc")])]})])],"derivedFrom":makeQuery(id+"F5.opExtrude","TWEAK_EDGE",EDGE,{"derivedFrom":[subQ0,makeQuery(id+"F4.imprint","IMPRINT",EDGE,{"derivedFrom":subQ1})]})});}
            var Q4;
            {var subQ0=sQuery(id+"F0.wireOp",EDGE,"E25.0");var subQ1=sQuery(id+"F0.wireOp",EDGE,"E25.1");var subQ2=sQuery(id+"F0.wireOp",EDGE,"E25.2");var subQ3=sQuery(id+"F0.wireOp",EDGE,"E25.3");var subQ4=sQuery(id+"F0.wireOp",EDGE,"E25.4");var subQ5=sQuery(id+"F0.wireOp",EDGE,"E25.5");var subQ6=sQuery(id+"F0.wireOp",EDGE,"E25.6");var subQ7=sQuery(id+"F0.wireOp",EDGE,"E25.7");Q4=makeQuery(id+"F8.boolean.opBoolean","INTERSECT",EDGE,{"derivedFrom":[makeQuery(id+"F5.boolean.opBoolean","SPLIT",FACE,{"disambiguationData":[TD([makeQuery(id+"F2.opExtrude","SWEPT_FACE",FACE,{"disambiguationData":[OSD([subQ0])]})])],"derivedFrom":makeQuery(id+"F3.boolean.opBoolean","COPY",FACE,{"derivedFrom":makeQuery(id+"F3.opExtrude","CAP_FACE",FACE,{"disambiguationData":[OSD([subQ0,subQ1,subQ2,subQ3,subQ4,subQ5,subQ6,subQ7])],"isStart":false})})}),makeQuery(id+"F8.opExtrude","SWEPT_FACE",FACE,{"disambiguationData":[OSD([sQuery(id+"F7.wireOp",EDGE,"E67")])]})]});}
            var Q5;
            Q5=makeQuery(id+"F8.boolean.opBoolean","INTERSECT",EDGE,{"disambiguationData":[OD(0.0)],"derivedFrom":[makeQuery(id+"F5.opExtrude","SWEPT_FACE",FACE,{"disambiguationData":[OSD([sQuery(id+"F4.wireOp",EDGE,"E30")])]}),makeQuery(id+"F8.opExtrude","SWEPT_FACE",FACE,{"disambiguationData":[OSD([sQuery(id+"F7.wireOp",EDGE,"E67")])]})]});
            fillet(context, id + "F14", {"entities" : qUnion([Q0, Q1, Q2, Q3, Q4, Q5]), "radius" : 3 * mm, "tangentPropagation" : true, "allowEdgeOverflow" : false});
        }
        {
            var Q0;
            Q0=makeQuery(id+"F1.opExtrude","CAP_EDGE",EDGE,{"disambiguationData":[OSD([sQuery(id+"F0.wireOp",EDGE,"E1.bottom")])],"isStart":false});
            fillet(context, id + "F15", {"entities" : qUnion([Q0]), "radius" : 2 * mm, "tangentPropagation" : true, "allowEdgeOverflow" : false});
        }
        {
            var Q0;
            {var subQ0=sQuery(id+"F0.wireOp",EDGE,"E21.filletArc");var subQ1=sQuery(id+"F0.wireOp",EDGE,"E7");var subQ2=sQuery(id+"F0.wireOp",EDGE,"E6");var subQ3=sQuery(id+"F0.wireOp",EDGE,"E5");var subQ4=sQuery(id+"F0.wireOp",EDGE,"E4");var subQ5=sQuery(id+"F0.wireOp",EDGE,"E22.filletArc");var subQ6=sQuery(id+"F0.wireOp",EDGE,"E1.bottom");var subQ7=sQuery(id+"F0.wireOp",EDGE,"E1.right");var subQ8=sQuery(id+"F0.wireOp",EDGE,"E1.top");var subQ9=sQuery(id+"F0.wireOp",EDGE,"E1.left");var subQ10=sQuery(id+"F0.wireOp",EDGE,"E23.filletArc");var subQ11=sQuery(id+"F0.wireOp",EDGE,"E24.filletArc");Q0=makeQuery(id+"F2.boolean.opBoolean","SPLIT",FACE,{"disambiguationData":[TD([makeQuery(id+"F1.opExtrude","SWEPT_FACE",FACE,{"disambiguationData":[OSD([subQ6])]})])],"derivedFrom":makeQuery(id+"F1.opExtrude","CAP_FACE",FACE,{"disambiguationData":[OSD([subQ6,subQ8,subQ9,subQ7,subQ4,subQ3,subQ2,subQ1,subQ0,subQ5,subQ10,subQ11])],"isStart":true})});}
            var sketch = newSketch(context, id + "F16", { "sketchPlane" : qUnion([Q0])});
            skLineSegment(sketch, "E79.0", {"start": v(90, -70) * mm, "end": v(90, 70) * mm});
            skArc(sketch, "E79.1", {"start": v(90, 70) * mm, "mid": v(87.07, 77.07) * mm, "end": v(80, 80) * mm});
            skLineSegment(sketch, "E79.2", {"start": v(-80, 80) * mm, "end": v(80, 80) * mm});
            skCircle(sketch, "E79.3", {"center": v(60, 53.33) * mm, "radius": 4 * mm});
            skArc(sketch, "E79.4", {"start": v(52.38, 47.01) * mm, "mid": v(0, 53.33) * mm, "end": v(-52.38, 47.01) * mm});
            skArc(sketch, "E79.5", {"start": v(60, 37.3) * mm, "mid": v(57.87, 43.47) * mm, "end": v(52.38, 47.01) * mm});
            skLineSegment(sketch, "E79.6", {"start": v(60, 37.3) * mm, "end": v(60, -37.3) * mm});
            skLineSegment(sketch, "E79.7", {"start": v(-60, 37.3) * mm, "end": v(-60, -37.3) * mm});
            skArc(sketch, "E79.8", {"start": v(-52.38, 47.01) * mm, "mid": v(-57.87, 43.47) * mm, "end": v(-60, 37.3) * mm});
            skArc(sketch, "E79.9", {"start": v(-80, 80) * mm, "mid": v(-87.07, 77.07) * mm, "end": v(-90, 70) * mm});
            skCircle(sketch, "E79.10", {"center": v(-60, 53.33) * mm, "radius": 4 * mm});
            skLineSegment(sketch, "E79.11", {"start": v(-90, -70) * mm, "end": v(-90, 70) * mm});
            skCircle(sketch, "E79.12", {"center": v(-60, -53.33) * mm, "radius": 4 * mm});
            skArc(sketch, "E79.13", {"start": v(-90, -70) * mm, "mid": v(-87.07, -77.07) * mm, "end": v(-80, -80) * mm});
            skLineSegment(sketch, "E79.14", {"start": v(-80, -80) * mm, "end": v(80, -80) * mm});
            skCircle(sketch, "E79.15", {"center": v(60, -53.33) * mm, "radius": 4 * mm});
            skArc(sketch, "E79.16", {"start": v(80, -80) * mm, "mid": v(87.07, -77.07) * mm, "end": v(90, -70) * mm});
            skArc(sketch, "E79.17", {"start": v(52.38, -47.01) * mm, "mid": v(57.87, -43.47) * mm, "end": v(60, -37.3) * mm});
            skArc(sketch, "E79.18", {"start": v(-52.38, -47.01) * mm, "mid": v(0, -53.33) * mm, "end": v(52.38, -47.01) * mm});
            skArc(sketch, "E79.19", {"start": v(-60, -37.3) * mm, "mid": v(-57.87, -43.47) * mm, "end": v(-52.38, -47.01) * mm});
            skLineSegment(sketch, "E80", {"start": v(0, 80) * mm, "end": v(0, 110) * mm, "construction": true});
            skCircle(sketch, "E81", {"center": v(0, 110) * mm, "radius": 6 * mm});
            skLineSegment(sketch, "E82", {"start": v(-15, 92.25) * mm, "end": v(-15, 110) * mm});
            skLineSegment(sketch, "E83", {"start": v(15, 110) * mm, "end": v(15, 92.25) * mm});
            skLineSegment(sketch, "E84", {"start": v(-15, 92.25) * mm, "end": v(-27.25, 80) * mm});
            skLineSegment(sketch, "E85", {"start": v(15, 92.25) * mm, "end": v(27.25, 80) * mm});
            skArc(sketch, "E86", {"start": v(-15, 110) * mm, "mid": v(0, 125) * mm, "end": v(15, 110) * mm});
            skLineSegment(sketch, "E87", {"start": v(0, 0) * mm, "end": v(-90, 0) * mm, "construction": true});
            skLineSegment(sketch, "E88", {"start": v(-90, 0) * mm, "end": v(90, 0) * mm, "construction": true});
            skLineSegment(sketch, "E89", {"start": v(90, 0) * mm, "end": v(0, 0) * mm, "construction": true});
            skLineSegment(sketch, "E90.MirrorCS", {"start": v(15, -110) * mm, "end": v(15, -92.25) * mm});
            skCircle(sketch, "E91.MirrorC", {"center": v(0, -110) * mm, "radius": 6 * mm});
            skLineSegment(sketch, "E92.MirrorCS", {"start": v(-15, -92.25) * mm, "end": v(-15, -110) * mm});
            skArc(sketch, "E93.MirrorCS", {"start": v(-15, -110) * mm, "mid": v(0, -125) * mm, "end": v(15, -110) * mm});
            skLineSegment(sketch, "E94.MirrorCS", {"start": v(-15, -92.25) * mm, "end": v(-27.25, -80) * mm});
            skLineSegment(sketch, "E95.MirrorCS", {"start": v(15, -92.25) * mm, "end": v(27.25, -80) * mm});
            skLineSegment(sketch, "E96.MirrorCS", {"start": v(0, -80) * mm, "end": v(0, -110) * mm, "construction": true});
            skSolve(sketch);
        }
        {
            var Q0;
            Q0=makeQuery(id+"F16.imprint","IMPRINT",FACE,{"disambiguationData":[TD([[makeQuery(id+"F16.imprint","IMPRINT",EDGE,{"derivedFrom":sQuery(id+"F16.wireOp",EDGE,"E81")}),-1.0]])]});
            var Q1;
            Q1=makeQuery(id+"F16.imprint","IMPRINT",FACE,{"disambiguationData":[TD([[makeQuery(id+"F16.imprint","IMPRINT",EDGE,{"derivedFrom":sQuery(id+"F16.wireOp",EDGE,"E90.MirrorCS")}),1.0]])]});
            var Q2;
            Q2=makeQuery(id+"F16.imprint","IMPRINT",FACE,{"disambiguationData":[TD([[makeQuery(id+"F16.imprint","IMPRINT",EDGE,{"derivedFrom":sQuery(id+"F16.wireOp",EDGE,"E79.0")}),1.0]])]});
            var Q3;
            Q3=makeQuery(id+"F2.opExtrude","CAP_FACE",FACE,{"disambiguationData":[OSD([sQuery(id+"F0.wireOp",EDGE,"E12"),sQuery(id+"F0.wireOp",EDGE,"E13"),sQuery(id+"F0.wireOp",EDGE,"E14"),sQuery(id+"F0.wireOp",EDGE,"E15"),sQuery(id+"F0.wireOp",EDGE,"E17.filletArc"),sQuery(id+"F0.wireOp",EDGE,"E18.filletArc"),sQuery(id+"F0.wireOp",EDGE,"E19.filletArc"),sQuery(id+"F0.wireOp",EDGE,"E20.filletArc"),sQuery(id+"F0.wireOp",EDGE,"E25.0"),sQuery(id+"F0.wireOp",EDGE,"E25.1"),sQuery(id+"F0.wireOp",EDGE,"E25.2"),sQuery(id+"F0.wireOp",EDGE,"E25.3"),sQuery(id+"F0.wireOp",EDGE,"E25.4"),sQuery(id+"F0.wireOp",EDGE,"E25.5"),sQuery(id+"F0.wireOp",EDGE,"E25.6"),sQuery(id+"F0.wireOp",EDGE,"E25.7")])],"isStart":false});
            extrude(context, id + "F17", {"entities" : qUnion([Q0, Q1, Q2]), "endBound" : BoundingType.UP_TO_SURFACE, "endBoundEntityFace" : qUnion([Q3]), "depth" : 25 * mm});
        }
    });
